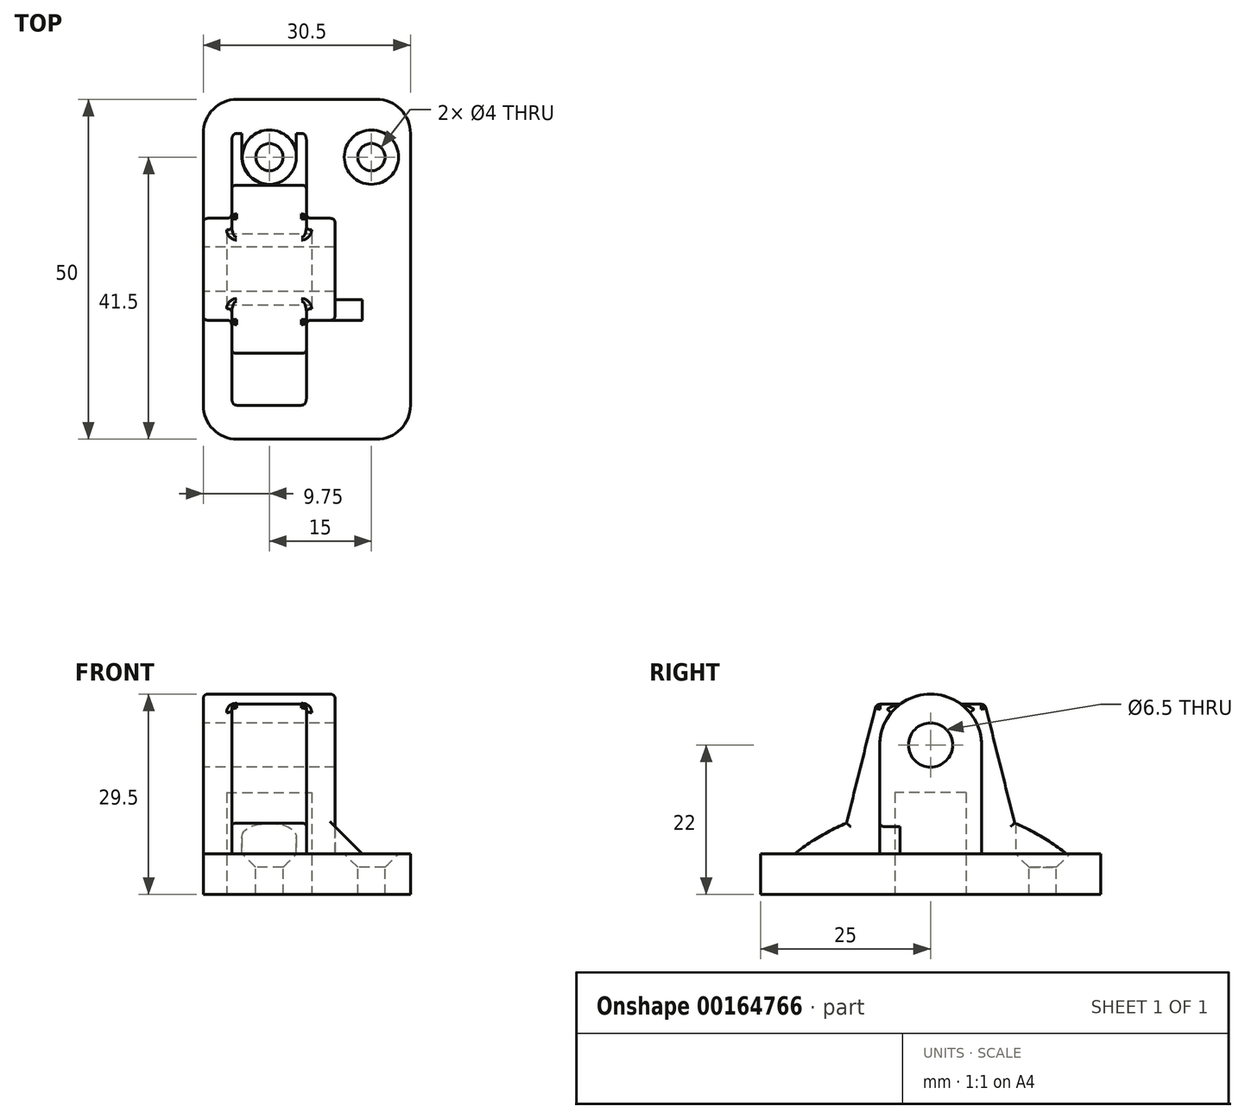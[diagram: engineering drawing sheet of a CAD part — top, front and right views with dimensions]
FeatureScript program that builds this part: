
annotation { "Feature Type Name" : "Feature", "Feature Type Description" : "" }
export const myFeature = defineFeature(function(context is Context, id is Id, definition is map)
    precondition{}
    {
        {
            var Q0;
            Q0=qCreatedBy(makeId("Top.planeOp"),FACE);
            var sketch = newSketch(context, id + "F0", { "sketchPlane" : qUnion([Q0])});
            skLineSegment(sketch, "E0.bottom", {"start": v(0, 0) * mm, "end": v(30.5, 0) * mm});
            skLineSegment(sketch, "E0.top", {"start": v(0, 50) * mm, "end": v(30.5, 50) * mm});
            skLineSegment(sketch, "E0.left", {"start": v(0, 0) * mm, "end": v(0, 50) * mm});
            skLineSegment(sketch, "E0.right", {"start": v(30.5, 0) * mm, "end": v(30.5, 50) * mm});
            skSolve(sketch);
        }
        {
            var Q0;
            Q0=makeQuery(id+"F0.imprint","IMPRINT",FACE,{"disambiguationData":[TD([[makeQuery(id+"F0.imprint","IMPRINT",EDGE,{"derivedFrom":sQuery(id+"F0.wireOp",EDGE,"E0.bottom")}),1.0]])]});
            extrude(context, id + "F1", {"entities" : qUnion([Q0]), "depth" : 6 * mm});
        }
        {
            var Q0;
            Q0=makeQuery(id+"F1.opExtrude","SWEPT_EDGE",EDGE,{"disambiguationData":[OSD([sQuery(id+"F0.wireOp",EDGE,"E0.top"),sQuery(id+"F0.wireOp",EDGE,"E0.right")])]});
            var Q1;
            Q1=makeQuery(id+"F1.opExtrude","SWEPT_EDGE",EDGE,{"disambiguationData":[OSD([sQuery(id+"F0.wireOp",EDGE,"E0.top"),sQuery(id+"F0.wireOp",EDGE,"E0.left")])]});
            var Q2;
            Q2=makeQuery(id+"F1.opExtrude","SWEPT_EDGE",EDGE,{"disambiguationData":[OSD([sQuery(id+"F0.wireOp",EDGE,"E0.bottom"),sQuery(id+"F0.wireOp",EDGE,"E0.left")])]});
            var Q3;
            Q3=makeQuery(id+"F1.opExtrude","SWEPT_EDGE",EDGE,{"disambiguationData":[OSD([sQuery(id+"F0.wireOp",EDGE,"E0.bottom"),sQuery(id+"F0.wireOp",EDGE,"E0.right")])]});
            fillet(context, id + "F2", {"entities" : qUnion([Q0, Q1, Q2, Q3]), "radius" : 5 * mm, "tangentPropagation" : true, "allowEdgeOverflow" : false});
        }
        {
            var Q0;
            Q0=qCreatedBy(makeId("Front.planeOp"),FACE);
            cPlane(context, id + "F3", {"entities" : qUnion([Q0]), "cplaneType" : CPlaneType.OFFSET, "offset" : 25 * mm, "oppositeDirection" : true, "width" : 150 * mm, "height" : 150 * mm});
        }
        {
            var Q0;
            Q0=qCreatedBy(makeId("Right.planeOp"),FACE);
            var sketch = newSketch(context, id + "F4", { "sketchPlane" : qUnion([Q0])});
            skLineSegment(sketch, "E1.top", {"start": v(32.5, 6) * mm, "end": v(17.5, 6) * mm});
            skLineSegment(sketch, "E1.left", {"start": v(32.5, 22) * mm, "end": v(32.5, 6) * mm});
            skLineSegment(sketch, "E1.right", {"start": v(17.5, 22) * mm, "end": v(17.5, 6) * mm});
            skArc(sketch, "E2", {"start": v(32.5, 22) * mm, "mid": v(25, 29.5) * mm, "end": v(17.5, 22) * mm});
            skSolve(sketch);
        }
        {
            var Q0;
            Q0=makeQuery(id+"F4.imprint","IMPRINT",FACE,{"disambiguationData":[TD([[makeQuery(id+"F4.imprint","IMPRINT",EDGE,{"derivedFrom":sQuery(id+"F4.wireOp",EDGE,"E1.top")}),-1.0]])]});
            extrude(context, id + "F5", {"entities" : qUnion([Q0]), "operationType" : NewBodyOperationType.ADD, "depth" : 19.4 * mm});
        }
        {
            var Q0;
            Q0=qCreatedBy(makeId("Right.planeOp"),FACE);
            cPlane(context, id + "F6", {"entities" : qUnion([Q0]), "cplaneType" : CPlaneType.OFFSET, "offset" : (19.4 / 2) * mm, "width" : 150 * mm, "height" : 150 * mm});
        }
        {
            var Q0;
            Q0=qCreatedBy(id+"F6.planeOp",FACE);
            var sketch = newSketch(context, id + "F7", { "sketchPlane" : qUnion([Q0])});
            skLineSegment(sketch, "E3", {"start": v(17, 28) * mm, "end": v(25, 28) * mm});
            skLineSegment(sketch, "E4", {"start": v(17, 28) * mm, "end": v(12.63, 10.52) * mm});
            skLineSegment(sketch, "E5", {"start": v(11.5, 6) * mm, "end": v(25, 6) * mm});
            skLineSegment(sketch, "E6.MirrorCS", {"start": v(38.5, 6) * mm, "end": v(25, 6) * mm});
            skLineSegment(sketch, "E7.MirrorCS", {"start": v(33, 28) * mm, "end": v(25, 28) * mm});
            skLineSegment(sketch, "E8.MirrorCS", {"start": v(33, 28) * mm, "end": v(37.37, 10.52) * mm});
            skLineSegment(sketch, "E9", {"start": v(-10.26, 6) * mm, "end": v(63.4, 6) * mm, "construction": true});
            skArc(sketch, "E10", {"start": v(45, 6) * mm, "mid": v(41.34, 8.52) * mm, "end": v(37.37, 10.52) * mm});
            skArc(sketch, "E11.trimOffspring", {"start": v(12.63, 10.52) * mm, "mid": v(8.66, 8.52) * mm, "end": v(5, 6) * mm});
            skLineSegment(sketch, "E12", {"start": v(5, 6) * mm, "end": v(45, 6) * mm});
            skSolve(sketch);
        }
        {
            var Q0;
            Q0=makeQuery(id+"F7.imprint","IMPRINT",FACE,{"disambiguationData":[TD([[makeQuery(id+"F7.imprint","IMPRINT",EDGE,{"derivedFrom":sQuery(id+"F7.wireOp",EDGE,"E3")}),-1.0]])]});
            extrude(context, id + "F8", {"entities" : qUnion([Q0]), "operationType" : NewBodyOperationType.ADD, "endBound" : BoundingType.SYMMETRIC, "depth" : 11 * mm});
        }
        {
            var Q0;
            Q0=makeQuery(id+"F5.boolean.opBoolean","MERGE",FACE,{"derivedFrom":[makeQuery(id+"F1.opExtrude","SWEPT_FACE",FACE,{"disambiguationData":[OSD([sQuery(id+"F0.wireOp",EDGE,"E0.left")])]}),makeQuery(id+"F5.opExtrude","CAP_FACE",FACE,{"disambiguationData":[OSD([sQuery(id+"F4.wireOp",EDGE,"E1.top"),sQuery(id+"F4.wireOp",EDGE,"E1.left"),sQuery(id+"F4.wireOp",EDGE,"E1.right"),sQuery(id+"F4.wireOp",EDGE,"E2")])],"isStart":true})]});
            var sketch = newSketch(context, id + "F9", { "sketchPlane" : qUnion([Q0])});
            skPoint(sketch, "E13", {"position": v(-25, 22) * mm});
            skSolve(sketch);
        }
        {
            var Q0;
            Q0=sQuery(id+"F9.wireOp",VERTEX,"E13");
            var Q1;
            Q1=makeQuery(id+"F1.opExtrude","SWEPT_BODY",BODY,{"disambiguationData":[OSD([sQuery(id+"F0.wireOp",EDGE,"E0.bottom"),sQuery(id+"F0.wireOp",EDGE,"E0.top"),sQuery(id+"F0.wireOp",EDGE,"E0.left"),sQuery(id+"F0.wireOp",EDGE,"E0.right")])]});
            hole(context, id + "F10", {"style" : HoleStyle.SIMPLE, "endStyle" : HoleEndStyle.THROUGH, "holeDiameter" : 6.5 * mm, "locations" : qUnion([Q0]), "scope" : qUnion([Q1]), "isTappedThrough" : true});
        }
        {
            var Q0;
            Q0=qCreatedBy(id+"F3.planeOp",FACE);
            cPlane(context, id + "F11", {"entities" : qUnion([Q0]), "cplaneType" : CPlaneType.OFFSET, "offset" : 7.5 * mm, "width" : 150 * mm, "height" : 150 * mm});
        }
        {
            var Q0;
            Q0=qCreatedBy(id+"F11.planeOp",FACE);
            var sketch = newSketch(context, id + "F12", { "sketchPlane" : qUnion([Q0])});
            skLineSegment(sketch, "E14", {"start": v(19.4, 10) * mm, "end": v(19.4, 6) * mm});
            skLineSegment(sketch, "E15", {"start": v(19.4, 6) * mm, "end": v(23.4, 6) * mm});
            skLineSegment(sketch, "E16", {"start": v(23.4, 6) * mm, "end": v(19.4, 10) * mm});
            skSolve(sketch);
        }
        {
            var Q0;
            Q0=makeQuery(id+"F12.imprint","IMPRINT",FACE,{"disambiguationData":[TD([[makeQuery(id+"F12.imprint","IMPRINT",EDGE,{"derivedFrom":sQuery(id+"F12.wireOp",EDGE,"E14")}),1.0]])]});
            extrude(context, id + "F13", {"entities" : qUnion([Q0]), "operationType" : NewBodyOperationType.ADD, "oppositeDirection" : true, "depth" : 3 * mm});
        }
        {
            var Q0;
            Q0=makeQuery(id+"F1.opExtrude","CAP_FACE",FACE,{"disambiguationData":[OSD([sQuery(id+"F0.wireOp",EDGE,"E0.bottom"),sQuery(id+"F0.wireOp",EDGE,"E0.top"),sQuery(id+"F0.wireOp",EDGE,"E0.left"),sQuery(id+"F0.wireOp",EDGE,"E0.right")])],"isStart":false});
            cPlane(context, id + "F14", {"entities" : qUnion([Q0]), "cplaneType" : CPlaneType.OFFSET, "offset" : 0 * mm, "width" : 150 * mm, "height" : 150 * mm});
        }
        {
            var Q0;
            Q0=makeQuery(id+"F1.opExtrude","CAP_FACE",FACE,{"disambiguationData":[OSD([sQuery(id+"F0.wireOp",EDGE,"E0.bottom"),sQuery(id+"F0.wireOp",EDGE,"E0.top"),sQuery(id+"F0.wireOp",EDGE,"E0.left"),sQuery(id+"F0.wireOp",EDGE,"E0.right")])],"isStart":false});
            var sketch = newSketch(context, id + "F15", { "sketchPlane" : qUnion([Q0])});
            skLineSegment(sketch, "E17", {"start": v(-17.4, 41.5) * mm, "end": v(51.74, 41.5) * mm, "construction": true});
            skPoint(sketch, "E18", {"position": v(24.75, 41.5) * mm});
            skPoint(sketch, "E19", {"position": v(9.75, 41.5) * mm});
            skSolve(sketch);
        }
        {
            var Q0;
            Q0=sQuery(id+"F15.wireOp",VERTEX,"E18");
            var Q1;
            Q1=makeQuery(id+"F1.opExtrude","SWEPT_BODY",BODY,{"disambiguationData":[OSD([sQuery(id+"F0.wireOp",EDGE,"E0.bottom"),sQuery(id+"F0.wireOp",EDGE,"E0.top"),sQuery(id+"F0.wireOp",EDGE,"E0.left"),sQuery(id+"F0.wireOp",EDGE,"E0.right")])]});
            hole(context, id + "F16", {"style" : HoleStyle.C_SINK, "endStyle" : HoleEndStyle.THROUGH, "holeDiameter" : 4 * mm, "cSinkDiameter" : 8 * mm, "cSinkAngle" : 90 * degree, "locations" : qUnion([Q0]), "scope" : qUnion([Q1]), "isTappedThrough" : true});
        }
        {
            var Q0;
            Q0=sQuery(id+"F15.wireOp",VERTEX,"E19");
            var Q1;
            Q1=makeQuery(id+"F1.opExtrude","SWEPT_BODY",BODY,{"disambiguationData":[OSD([sQuery(id+"F0.wireOp",EDGE,"E0.bottom"),sQuery(id+"F0.wireOp",EDGE,"E0.top"),sQuery(id+"F0.wireOp",EDGE,"E0.left"),sQuery(id+"F0.wireOp",EDGE,"E0.right")])]});
            hole(context, id + "F17", {"style" : HoleStyle.C_SINK, "endStyle" : HoleEndStyle.THROUGH, "holeDiameter" : 4 * mm, "cSinkDiameter" : 8 * mm, "cSinkAngle" : 90 * degree, "locations" : qUnion([Q0]), "scope" : qUnion([Q1]), "isTappedThrough" : true});
        }
        {
            var Q0;
            Q0=qCreatedBy(id+"F14.planeOp",FACE);
            var sketch = newSketch(context, id + "F18", { "sketchPlane" : qUnion([Q0])});
            skLineSegment(sketch, "E20.bottom", {"start": v(5.7, 45) * mm, "end": v(13.7, 45) * mm});
            skLineSegment(sketch, "E20.left", {"start": v(5.7, 45) * mm, "end": v(5.7, 41.5) * mm});
            skLineSegment(sketch, "E20.right", {"start": v(13.7, 45) * mm, "end": v(13.7, 41.5) * mm});
            skArc(sketch, "E21", {"start": v(5.7, 41.5) * mm, "mid": v(9.7, 37.5) * mm, "end": v(13.7, 41.5) * mm});
            skSolve(sketch);
        }
        {
            var Q0;
            Q0 = qSketchRegion(id + "F18", true);
            extrude(context, id + "F19", {"entities" : qUnion([Q0]), "operationType" : NewBodyOperationType.REMOVE, "endBound" : BoundingType.THROUGH_ALL, "depth" : 25 * mm});
        }
        {
            var Q0;
            Q0=makeQuery(id+"F5.opExtrude","CAP_EDGE",EDGE,{"disambiguationData":[OSD([sQuery(id+"F4.wireOp",EDGE,"E2")])],"isStart":false});
            var Q1;
            Q1=makeQuery(id+"F5.opExtrude","CAP_EDGE",EDGE,{"disambiguationData":[OSD([sQuery(id+"F4.wireOp",EDGE,"E1.right")])],"isStart":false});
            var Q2;
            Q2=makeQuery(id+"F5.opExtrude","CAP_EDGE",EDGE,{"disambiguationData":[OSD([sQuery(id+"F4.wireOp",EDGE,"E1.left")])],"isStart":false});
            var Q3;
            Q3=makeQuery(id+"F8.opExtrude","CAP_EDGE",EDGE,{"disambiguationData":[OSD([sQuery(id+"F7.wireOp",EDGE,"E4")])],"isStart":false});
            var Q4;
            {var subQ0=sQuery(id+"F7.wireOp",EDGE,"E7.MirrorCS");var subQ1=sQuery(id+"F7.wireOp",EDGE,"E4");var subQ2=sQuery(id+"F7.wireOp",EDGE,"E3");Q4=makeQuery(id+"F8.boolean.opBoolean","SPLIT",EDGE,{"disambiguationData":[TD([makeQuery(id+"F8.opExtrude","SWEPT_FACE",FACE,{"disambiguationData":[OSD([subQ1])]})])],"derivedFrom":makeQuery(id+"F8.opExtrude","CAP_EDGE",EDGE,{"disambiguationData":[OSD([subQ2,subQ0])],"isStart":false})});}
            var Q5;
            Q5=makeQuery(id+"F8.boolean.opBoolean","INTERSECT",EDGE,{"disambiguationData":[OD(0.0)],"derivedFrom":[makeQuery(id+"F5.opExtrude","SWEPT_FACE",FACE,{"disambiguationData":[OSD([sQuery(id+"F4.wireOp",EDGE,"E2")])]}),makeQuery(id+"F8.opExtrude","SWEPT_FACE",FACE,{"disambiguationData":[OSD([sQuery(id+"F7.wireOp",EDGE,"E3"),sQuery(id+"F7.wireOp",EDGE,"E7.MirrorCS")])]})]});
            var Q6;
            {var subQ0=sQuery(id+"F7.wireOp",EDGE,"E7.MirrorCS");var subQ1=sQuery(id+"F7.wireOp",EDGE,"E4");var subQ2=sQuery(id+"F7.wireOp",EDGE,"E3");Q6=makeQuery(id+"F8.boolean.opBoolean","SPLIT",EDGE,{"disambiguationData":[TD([makeQuery(id+"F8.opExtrude","SWEPT_FACE",FACE,{"disambiguationData":[OSD([subQ1])]})])],"derivedFrom":makeQuery(id+"F8.opExtrude","CAP_EDGE",EDGE,{"disambiguationData":[OSD([subQ2,subQ0])],"isStart":true})});}
            var Q7;
            Q7=makeQuery(id+"F8.opExtrude","CAP_EDGE",EDGE,{"disambiguationData":[OSD([sQuery(id+"F7.wireOp",EDGE,"E4")])],"isStart":true});
            var Q8;
            Q8=makeQuery(id+"F8.boolean.opBoolean","INTERSECT",EDGE,{"derivedFrom":[makeQuery(id+"F5.opExtrude","SWEPT_FACE",FACE,{"disambiguationData":[OSD([sQuery(id+"F4.wireOp",EDGE,"E1.right")])]}),makeQuery(id+"F8.opExtrude","CAP_FACE",FACE,{"disambiguationData":[OSD([sQuery(id+"F7.wireOp",EDGE,"E3"),sQuery(id+"F7.wireOp",EDGE,"E4"),sQuery(id+"F7.wireOp",EDGE,"E7.MirrorCS"),sQuery(id+"F7.wireOp",EDGE,"E8.MirrorCS"),sQuery(id+"F7.wireOp",EDGE,"E10"),sQuery(id+"F7.wireOp",EDGE,"E11.trimOffspring"),sQuery(id+"F7.wireOp",EDGE,"E12")])],"isStart":false})]});
            var Q9;
            Q9=makeQuery(id+"F8.boolean.opBoolean","INTERSECT",EDGE,{"disambiguationData":[OD(0.0)],"derivedFrom":[makeQuery(id+"F5.opExtrude","SWEPT_FACE",FACE,{"disambiguationData":[OSD([sQuery(id+"F4.wireOp",EDGE,"E2")])]}),makeQuery(id+"F8.opExtrude","CAP_FACE",FACE,{"disambiguationData":[OSD([sQuery(id+"F7.wireOp",EDGE,"E3"),sQuery(id+"F7.wireOp",EDGE,"E4"),sQuery(id+"F7.wireOp",EDGE,"E7.MirrorCS"),sQuery(id+"F7.wireOp",EDGE,"E8.MirrorCS"),sQuery(id+"F7.wireOp",EDGE,"E10"),sQuery(id+"F7.wireOp",EDGE,"E11.trimOffspring"),sQuery(id+"F7.wireOp",EDGE,"E12")])],"isStart":false})]});
            var Q10;
            Q10=makeQuery(id+"F8.opExtrude","CAP_EDGE",EDGE,{"disambiguationData":[OSD([sQuery(id+"F7.wireOp",EDGE,"E11.trimOffspring")])],"isStart":false});
            var Q11;
            Q11=makeQuery(id+"F8.opExtrude","CAP_EDGE",EDGE,{"disambiguationData":[OSD([sQuery(id+"F7.wireOp",EDGE,"E11.trimOffspring")])],"isStart":true});
            var Q12;
            Q12=makeQuery(id+"F8.boolean.opBoolean","INTERSECT",EDGE,{"disambiguationData":[OD(0.0)],"derivedFrom":[makeQuery(id+"F5.opExtrude","SWEPT_FACE",FACE,{"disambiguationData":[OSD([sQuery(id+"F4.wireOp",EDGE,"E2")])]}),makeQuery(id+"F8.opExtrude","CAP_FACE",FACE,{"disambiguationData":[OSD([sQuery(id+"F7.wireOp",EDGE,"E3"),sQuery(id+"F7.wireOp",EDGE,"E4"),sQuery(id+"F7.wireOp",EDGE,"E7.MirrorCS"),sQuery(id+"F7.wireOp",EDGE,"E8.MirrorCS"),sQuery(id+"F7.wireOp",EDGE,"E10"),sQuery(id+"F7.wireOp",EDGE,"E11.trimOffspring"),sQuery(id+"F7.wireOp",EDGE,"E12")])],"isStart":true})]});
            var Q13;
            Q13=makeQuery(id+"F5.opExtrude","CAP_EDGE",EDGE,{"disambiguationData":[OSD([sQuery(id+"F4.wireOp",EDGE,"E1.right")])],"isStart":true});
            var Q14;
            Q14=makeQuery(id+"F5.opExtrude","CAP_EDGE",EDGE,{"disambiguationData":[OSD([sQuery(id+"F4.wireOp",EDGE,"E2")])],"isStart":true});
            var Q15;
            Q15=makeQuery(id+"F5.opExtrude","CAP_EDGE",EDGE,{"disambiguationData":[OSD([sQuery(id+"F4.wireOp",EDGE,"E1.left")])],"isStart":true});
            var Q16;
            {var subQ0=sQuery(id+"F7.wireOp",EDGE,"E8.MirrorCS");var subQ1=sQuery(id+"F7.wireOp",EDGE,"E7.MirrorCS");var subQ2=sQuery(id+"F7.wireOp",EDGE,"E3");Q16=makeQuery(id+"F8.boolean.opBoolean","SPLIT",EDGE,{"disambiguationData":[TD([makeQuery(id+"F8.opExtrude","SWEPT_FACE",FACE,{"disambiguationData":[OSD([subQ0])]})])],"derivedFrom":makeQuery(id+"F8.opExtrude","CAP_EDGE",EDGE,{"disambiguationData":[OSD([subQ2,subQ1])],"isStart":true})});}
            var Q17;
            Q17=makeQuery(id+"F8.boolean.opBoolean","INTERSECT",EDGE,{"disambiguationData":[OD(1.0)],"derivedFrom":[makeQuery(id+"F5.opExtrude","SWEPT_FACE",FACE,{"disambiguationData":[OSD([sQuery(id+"F4.wireOp",EDGE,"E2")])]}),makeQuery(id+"F8.opExtrude","SWEPT_FACE",FACE,{"disambiguationData":[OSD([sQuery(id+"F7.wireOp",EDGE,"E3"),sQuery(id+"F7.wireOp",EDGE,"E7.MirrorCS")])]})]});
            var Q18;
            {var subQ0=sQuery(id+"F7.wireOp",EDGE,"E8.MirrorCS");var subQ1=sQuery(id+"F7.wireOp",EDGE,"E7.MirrorCS");var subQ2=sQuery(id+"F7.wireOp",EDGE,"E3");Q18=makeQuery(id+"F8.boolean.opBoolean","SPLIT",EDGE,{"disambiguationData":[TD([makeQuery(id+"F8.opExtrude","SWEPT_FACE",FACE,{"disambiguationData":[OSD([subQ0])]})])],"derivedFrom":makeQuery(id+"F8.opExtrude","CAP_EDGE",EDGE,{"disambiguationData":[OSD([subQ2,subQ1])],"isStart":false})});}
            var Q19;
            Q19=makeQuery(id+"F8.opExtrude","CAP_EDGE",EDGE,{"disambiguationData":[OSD([sQuery(id+"F7.wireOp",EDGE,"E8.MirrorCS")])],"isStart":true});
            var Q20;
            Q20=makeQuery(id+"F8.opExtrude","CAP_EDGE",EDGE,{"disambiguationData":[OSD([sQuery(id+"F7.wireOp",EDGE,"E10")])],"isStart":true});
            var Q21;
            Q21=makeQuery(id+"F8.opExtrude","SWEPT_EDGE",EDGE,{"disambiguationData":[OSD([sQuery(id+"F7.wireOp",EDGE,"E7.MirrorCS"),sQuery(id+"F7.wireOp",EDGE,"E8.MirrorCS")])]});
            var Q22;
            Q22=makeQuery(id+"F8.opExtrude","CAP_EDGE",EDGE,{"disambiguationData":[OSD([sQuery(id+"F7.wireOp",EDGE,"E8.MirrorCS")])],"isStart":false});
            var Q23;
            Q23=makeQuery(id+"F8.opExtrude","CAP_EDGE",EDGE,{"disambiguationData":[OSD([sQuery(id+"F7.wireOp",EDGE,"E10")])],"isStart":false});
            var Q24;
            Q24=makeQuery(id+"F8.boolean.opBoolean","INTERSECT",EDGE,{"disambiguationData":[OD(1.0)],"derivedFrom":[makeQuery(id+"F5.opExtrude","SWEPT_FACE",FACE,{"disambiguationData":[OSD([sQuery(id+"F4.wireOp",EDGE,"E2")])]}),makeQuery(id+"F8.opExtrude","CAP_FACE",FACE,{"disambiguationData":[OSD([sQuery(id+"F7.wireOp",EDGE,"E3"),sQuery(id+"F7.wireOp",EDGE,"E4"),sQuery(id+"F7.wireOp",EDGE,"E7.MirrorCS"),sQuery(id+"F7.wireOp",EDGE,"E8.MirrorCS"),sQuery(id+"F7.wireOp",EDGE,"E10"),sQuery(id+"F7.wireOp",EDGE,"E11.trimOffspring"),sQuery(id+"F7.wireOp",EDGE,"E12")])],"isStart":false})]});
            var Q25;
            Q25=makeQuery(id+"F8.boolean.opBoolean","INTERSECT",EDGE,{"derivedFrom":[makeQuery(id+"F5.opExtrude","SWEPT_FACE",FACE,{"disambiguationData":[OSD([sQuery(id+"F4.wireOp",EDGE,"E1.left")])]}),makeQuery(id+"F8.opExtrude","CAP_FACE",FACE,{"disambiguationData":[OSD([sQuery(id+"F7.wireOp",EDGE,"E3"),sQuery(id+"F7.wireOp",EDGE,"E4"),sQuery(id+"F7.wireOp",EDGE,"E7.MirrorCS"),sQuery(id+"F7.wireOp",EDGE,"E8.MirrorCS"),sQuery(id+"F7.wireOp",EDGE,"E10"),sQuery(id+"F7.wireOp",EDGE,"E11.trimOffspring"),sQuery(id+"F7.wireOp",EDGE,"E12")])],"isStart":false})]});
            var Q26;
            Q26=makeQuery(id+"F8.opExtrude","SWEPT_EDGE",EDGE,{"disambiguationData":[OSD([sQuery(id+"F7.wireOp",EDGE,"E3"),sQuery(id+"F7.wireOp",EDGE,"E4")])]});
            var Q27;
            Q27=makeQuery(id+"F8.boolean.opBoolean","INTERSECT",EDGE,{"disambiguationData":[OD(1.0)],"derivedFrom":[makeQuery(id+"F5.opExtrude","SWEPT_FACE",FACE,{"disambiguationData":[OSD([sQuery(id+"F4.wireOp",EDGE,"E2")])]}),makeQuery(id+"F8.opExtrude","CAP_FACE",FACE,{"disambiguationData":[OSD([sQuery(id+"F7.wireOp",EDGE,"E3"),sQuery(id+"F7.wireOp",EDGE,"E4"),sQuery(id+"F7.wireOp",EDGE,"E7.MirrorCS"),sQuery(id+"F7.wireOp",EDGE,"E8.MirrorCS"),sQuery(id+"F7.wireOp",EDGE,"E10"),sQuery(id+"F7.wireOp",EDGE,"E11.trimOffspring"),sQuery(id+"F7.wireOp",EDGE,"E12")])],"isStart":true})]});
            var Q28;
            Q28=makeQuery(id+"F8.boolean.opBoolean","INTERSECT",EDGE,{"derivedFrom":[makeQuery(id+"F5.opExtrude","SWEPT_FACE",FACE,{"disambiguationData":[OSD([sQuery(id+"F4.wireOp",EDGE,"E1.left")])]}),makeQuery(id+"F8.opExtrude","CAP_FACE",FACE,{"disambiguationData":[OSD([sQuery(id+"F7.wireOp",EDGE,"E3"),sQuery(id+"F7.wireOp",EDGE,"E4"),sQuery(id+"F7.wireOp",EDGE,"E7.MirrorCS"),sQuery(id+"F7.wireOp",EDGE,"E8.MirrorCS"),sQuery(id+"F7.wireOp",EDGE,"E10"),sQuery(id+"F7.wireOp",EDGE,"E11.trimOffspring"),sQuery(id+"F7.wireOp",EDGE,"E12")])],"isStart":true})]});
            fillet(context, id + "F20", {"entities" : qUnion([Q0, Q1, Q2, Q3, Q4, Q5, Q6, Q7, Q8, Q9, Q10, Q11, Q12, Q13, Q14, Q15, Q16, Q17, Q18, Q19, Q20, Q21, Q22, Q23, Q24, Q25, Q26, Q27, Q28]), "radius" : 0.75 * mm, "tangentPropagation" : true, "rho" : 0.5, "crossSection" : FilletCrossSection.CONIC, "allowEdgeOverflow" : false});
        }
        {
            var Q0;
            Q0=makeQuery(id+"F1.opExtrude","CAP_FACE",FACE,{"disambiguationData":[OSD([sQuery(id+"F0.wireOp",EDGE,"E0.bottom"),sQuery(id+"F0.wireOp",EDGE,"E0.top"),sQuery(id+"F0.wireOp",EDGE,"E0.left"),sQuery(id+"F0.wireOp",EDGE,"E0.right")])],"isStart":true});
            var sketch = newSketch(context, id + "F21", { "sketchPlane" : qUnion([Q0])});
            skLineSegment(sketch, "E22.bottom", {"start": v(3.45, -30.25) * mm, "end": v(15.95, -30.25) * mm});
            skLineSegment(sketch, "E22.top", {"start": v(3.45, -19.75) * mm, "end": v(15.95, -19.75) * mm});
            skLineSegment(sketch, "E22.left", {"start": v(3.45, -30.25) * mm, "end": v(3.45, -19.75) * mm});
            skLineSegment(sketch, "E22.right", {"start": v(15.95, -30.25) * mm, "end": v(15.95, -19.75) * mm});
            skSolve(sketch);
        }
        {
            var Q0;
            Q0=makeQuery(id+"F21.imprint","IMPRINT",FACE,{"disambiguationData":[TD([[makeQuery(id+"F21.imprint","IMPRINT",EDGE,{"derivedFrom":sQuery(id+"F21.wireOp",EDGE,"E22.bottom")}),1.0]])]});
            extrude(context, id + "F22", {"entities" : qUnion([Q0]), "operationType" : NewBodyOperationType.REMOVE, "oppositeDirection" : true, "depth" : 15 * mm});
        }
    });
